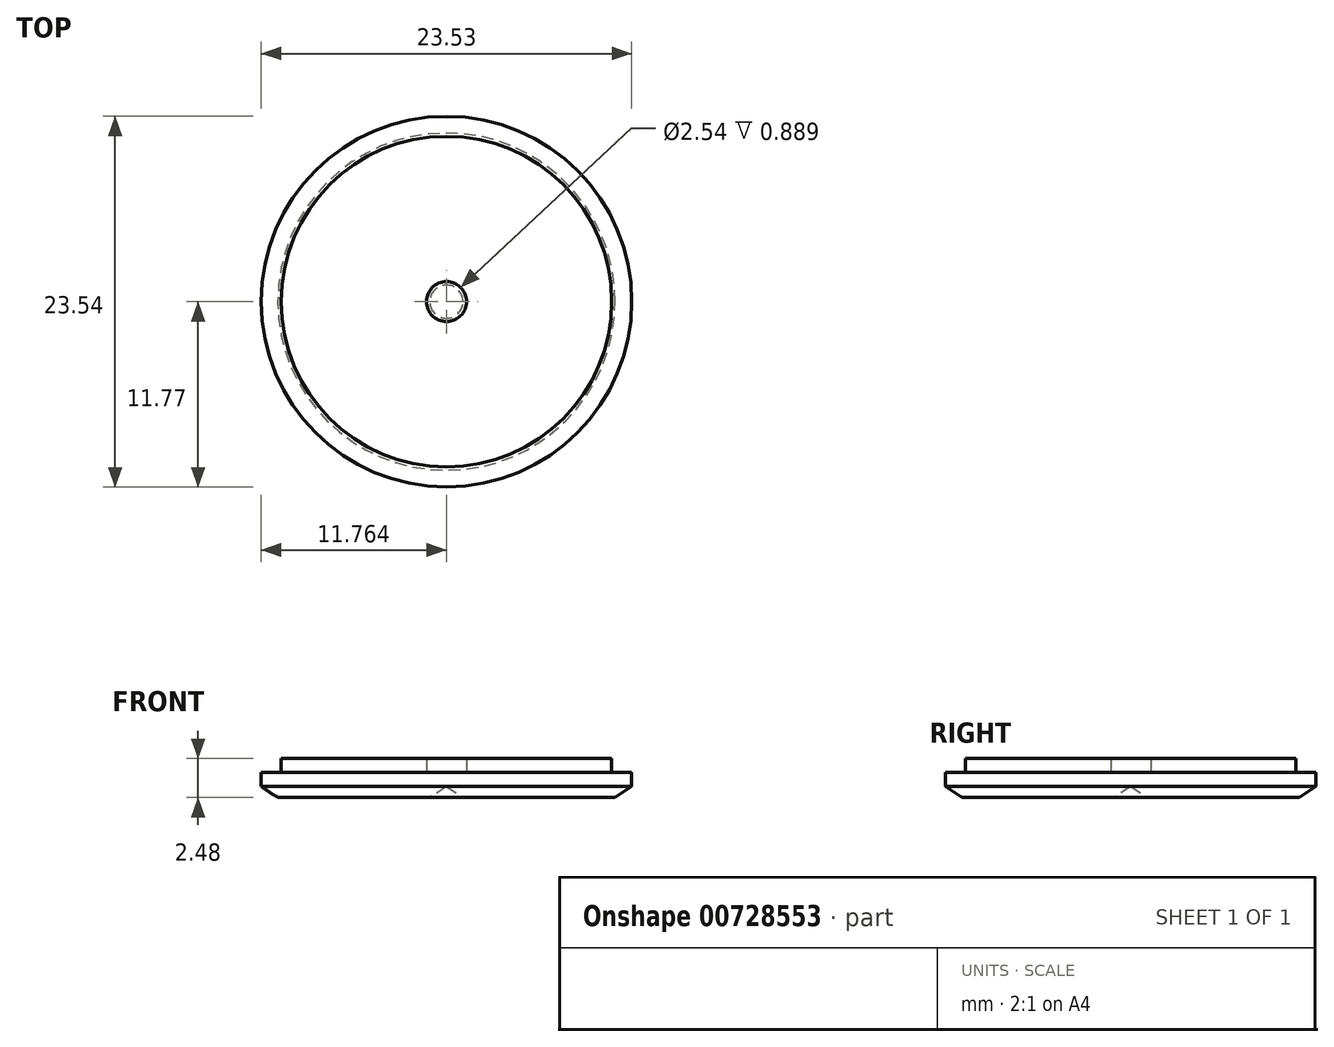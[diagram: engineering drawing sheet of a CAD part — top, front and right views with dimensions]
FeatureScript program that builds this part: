
annotation { "Feature Type Name" : "Feature", "Feature Type Description" : "" }
export const myFeature = defineFeature(function(context is Context, id is Id, definition is map)
    precondition{}
    {
        {
            var Q0;
            Q0=qCreatedBy(makeId("Front.planeOp"),FACE);
            var sketch = newSketch(context, id + "F0", { "sketchPlane" : qUnion([Q0])});
            skLineSegment(sketch, "E0", {"start": v(0, 0) * mm, "end": v(-4.83, 0) * mm});
            skLineSegment(sketch, "E1", {"start": v(0, 0) * mm, "end": v(4.83, 0) * mm});
            skLineSegment(sketch, "E2", {"start": v(4.83, 0) * mm, "end": v(5.88, 0.7) * mm});
            skLineSegment(sketch, "E3", {"start": v(-5.88, 0.7) * mm, "end": v(-4.83, 0) * mm});
            skLineSegment(sketch, "E4", {"start": v(-5.88, 0.7) * mm, "end": v(-5.88, 1.6) * mm});
            skLineSegment(sketch, "E5", {"start": v(5.88, 0.7) * mm, "end": v(5.88, 1.6) * mm});
            skLineSegment(sketch, "E6", {"start": v(-5.88, 1.6) * mm, "end": v(-4.61, 1.6) * mm});
            skLineSegment(sketch, "E7", {"start": v(5.88, 1.6) * mm, "end": v(4.61, 1.6) * mm});
            skLineSegment(sketch, "E8", {"start": v(-4.61, 1.6) * mm, "end": v(-4.61, 2.48) * mm});
            skLineSegment(sketch, "E9", {"start": v(4.61, 1.6) * mm, "end": v(4.61, 2.48) * mm});
            skLineSegment(sketch, "E10", {"start": v(4.61, 2.48) * mm, "end": v(-4.61, 2.48) * mm});
            skLineSegment(sketch, "E11", {"start": v(0, 0) * mm, "end": v(0, 2.48) * mm});
            skSolve(sketch);
        }
        {
            var Q0;
            Q0 = qSketchRegion(id + "F0", true);
            var Q1;
            Q1=sQuery(id+"F0.wireOp",EDGE,"E5");
            revolve(context, id + "F1", {"surfaceOperationType" : NewSurfaceOperationType.NEW, "entities" : qUnion([Q0]), "axis" : qUnion([Q1]), "revolveType" : RevolveType.FULL});
        }
    });
